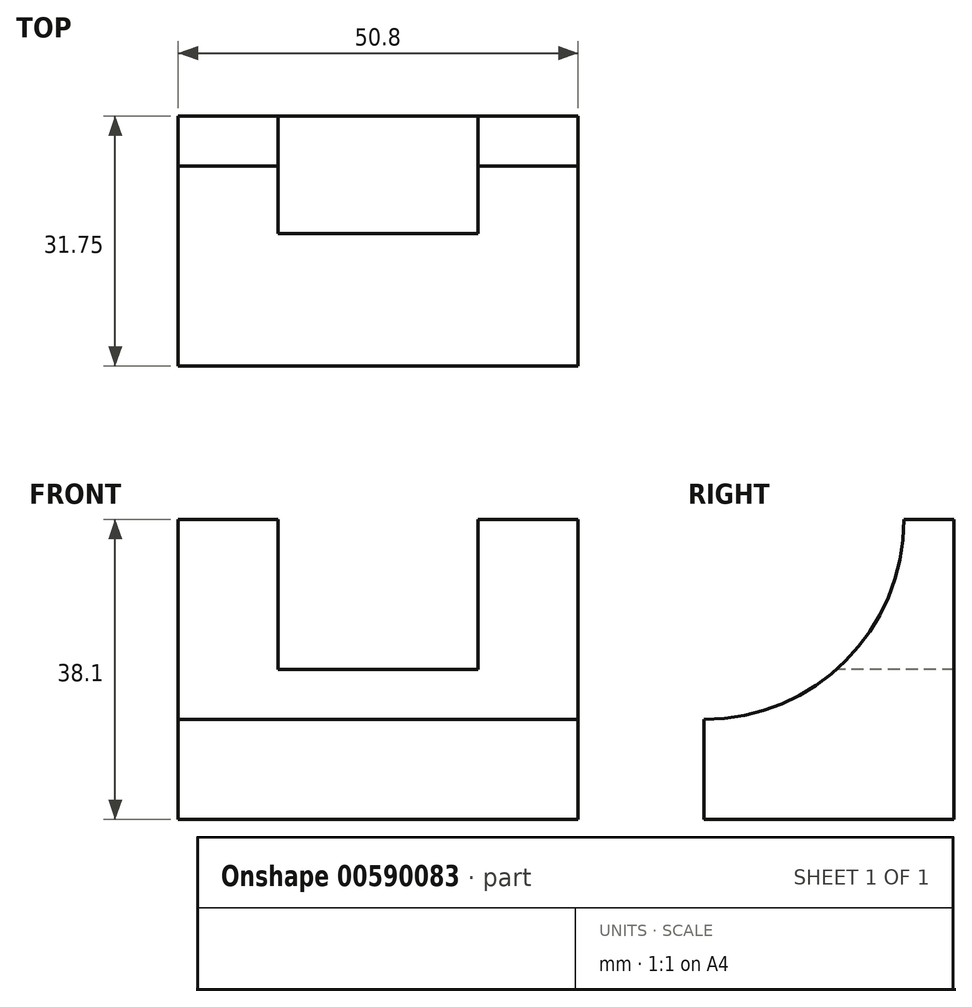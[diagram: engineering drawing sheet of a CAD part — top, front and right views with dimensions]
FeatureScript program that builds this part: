
annotation { "Feature Type Name" : "Feature", "Feature Type Description" : "" }
export const myFeature = defineFeature(function(context is Context, id is Id, definition is map)
    precondition{}
    {
        {
            var Q0;
            Q0=qCreatedBy(makeId("Front.planeOp"),FACE);
            var sketch = newSketch(context, id + "F0", { "sketchPlane" : qUnion([Q0])});
            skLineSegment(sketch, "E0.bottom", {"start": v(-64.97, 52.61) * mm, "end": v(-14.17, 52.61) * mm});
            skLineSegment(sketch, "E0.top", {"start": v(-64.97, 14.51) * mm, "end": v(-14.17, 14.51) * mm});
            skLineSegment(sketch, "E0.left", {"start": v(-64.97, 52.61) * mm, "end": v(-64.97, 14.51) * mm});
            skLineSegment(sketch, "E0.right", {"start": v(-14.17, 52.61) * mm, "end": v(-14.17, 14.51) * mm});
            skSolve(sketch);
        }
        {
            var Q0;
            Q0=makeQuery(id+"F0.imprint","IMPRINT",FACE,{"disambiguationData":[TD([[makeQuery(id+"F0.imprint","IMPRINT",EDGE,{"derivedFrom":sQuery(id+"F0.wireOp",EDGE,"E0.bottom")}),-1.0]])]});
            extrude(context, id + "F1", {"entities" : qUnion([Q0]), "depth" : 31.75 * mm, "offsetDistance" : 25.4 * mm});
        }
        {
            var Q0;
            Q0=makeQuery(id+"F1.opExtrude","CAP_FACE",FACE,{"disambiguationData":[OSD([sQuery(id+"F0.wireOp",EDGE,"E0.bottom"),sQuery(id+"F0.wireOp",EDGE,"E0.top"),sQuery(id+"F0.wireOp",EDGE,"E0.left"),sQuery(id+"F0.wireOp",EDGE,"E0.right")])],"isStart":false});
            var sketch = newSketch(context, id + "F2", { "sketchPlane" : qUnion([Q0])});
            skLineSegment(sketch, "E1", {"start": v(-52.27, 52.61) * mm, "end": v(-52.27, 33.56) * mm});
            skLineSegment(sketch, "E2", {"start": v(-52.27, 33.56) * mm, "end": v(-26.87, 33.56) * mm});
            skLineSegment(sketch, "E3", {"start": v(-26.87, 33.56) * mm, "end": v(-26.87, 52.61) * mm});
            skSolve(sketch);
        }
        {
            var Q0;
            {var subQ0=sQuery(id+"F2.wireOp",EDGE,"E1");Q0=makeQuery(id+"F2.imprint","IMPRINT",FACE,{"disambiguationData":[TD([[makeQuery(id+"F2.imprint","IMPRINT",EDGE,{"derivedFrom":subQ0}),1.0]])]});}
            extrude(context, id + "F3", {"entities" : qUnion([Q0]), "operationType" : NewBodyOperationType.REMOVE, "endBound" : BoundingType.THROUGH_ALL, "oppositeDirection" : true, "depth" : 25.4 * mm, "offsetDistance" : 25.4 * mm});
        }
        {
            var Q0;
            Q0=makeQuery(id+"F1.opExtrude","SWEPT_FACE",FACE,{"disambiguationData":[OSD([sQuery(id+"F0.wireOp",EDGE,"E0.right")])]});
            var sketch = newSketch(context, id + "F4", { "sketchPlane" : qUnion([Q0])});
            skCircle(sketch, "E4", {"center": v(-31.75, 52.61) * mm, "radius": 25.4 * mm});
            skSolve(sketch);
        }
        {
            var Q0;
            {var subQ0=sQuery(id+"F4.wireOp",EDGE,"E4");var subQ1=sQuery(id+"F0.wireOp",EDGE,"E0.right");var subQ4=makeQuery(id+"F1.opExtrude","CAP_EDGE",EDGE,{"disambiguationData":[OSD([subQ1])],"isStart":false});var subQ5=makeQuery(id+"F4.imprint","INTERSECT",VERTEX,{"derivedFrom":[subQ4,subQ0]});Q0=makeQuery(id+"F4.imprint","IMPRINT",FACE,{"disambiguationData":[TD([[makeQuery(id+"F4.imprint","IMPRINT",EDGE,{"disambiguationData":[TD([[subQ5,-1.0]])],"derivedFrom":subQ0}),1.0]])]});}
            extrude(context, id + "F5", {"entities" : qUnion([Q0]), "operationType" : NewBodyOperationType.REMOVE, "endBound" : BoundingType.THROUGH_ALL, "oppositeDirection" : true, "depth" : 25.4 * mm, "offsetDistance" : 25.4 * mm});
        }
    });
